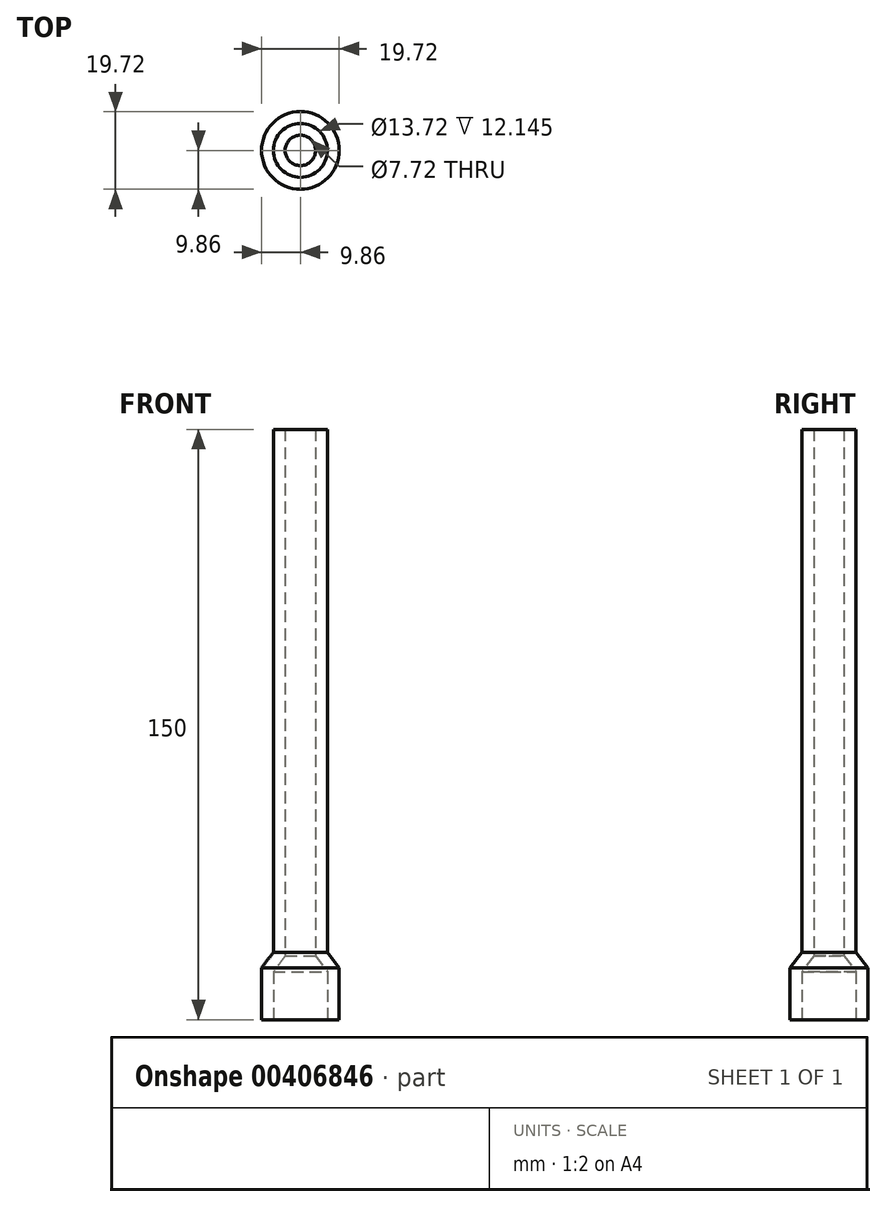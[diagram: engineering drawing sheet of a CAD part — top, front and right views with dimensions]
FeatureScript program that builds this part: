
annotation { "Feature Type Name" : "Feature", "Feature Type Description" : "" }
export const myFeature = defineFeature(function(context is Context, id is Id, definition is map)
    precondition{}
    {
        {
            var Q0;
            Q0=qCreatedBy(makeId("Front.planeOp"),FACE);
            var sketch = newSketch(context, id + "F0", { "sketchPlane" : qUnion([Q0])});
            skLineSegment(sketch, "E0", {"start": v(-9.86, 0) * mm, "end": v(-9.86, 13.14) * mm});
            skLineSegment(sketch, "E1", {"start": v(-9.86, 13.14) * mm, "end": v(-6.86, 17.14) * mm});
            skLineSegment(sketch, "E2", {"start": v(-6.86, 17.14) * mm, "end": v(-6.86, 150) * mm});
            skLineSegment(sketch, "E3.1", {"start": v(-3.86, 16.14) * mm, "end": v(-3.86, 150) * mm});
            skLineSegment(sketch, "E3.2", {"start": v(-6.86, 12.14) * mm, "end": v(-3.86, 16.14) * mm});
            skLineSegment(sketch, "E3.3", {"start": v(-6.86, 0) * mm, "end": v(-6.86, 12.14) * mm});
            skLineSegment(sketch, "E4", {"start": v(-6.86, 150) * mm, "end": v(-3.86, 150) * mm});
            skLineSegment(sketch, "E5", {"start": v(-9.86, 0) * mm, "end": v(-6.86, 0) * mm});
            skLineSegment(sketch, "E6", {"start": v(0, 0) * mm, "end": v(0, 75.73) * mm, "construction": true});
            skSolve(sketch);
        }
        {
            var Q0;
            Q0=makeQuery(id+"F0.imprint","IMPRINT",FACE,{"disambiguationData":[TD([[makeQuery(id+"F0.imprint","IMPRINT",EDGE,{"derivedFrom":sQuery(id+"F0.wireOp",EDGE,"E0")}),-1.0]])]});
            var Q1;
            Q1=sQuery(id+"F0.wireOp",EDGE,"E6");
            revolve(context, id + "F1", {"entities" : qUnion([Q0]), "axis" : qUnion([Q1]), "revolveType" : RevolveType.FULL});
        }
    });
